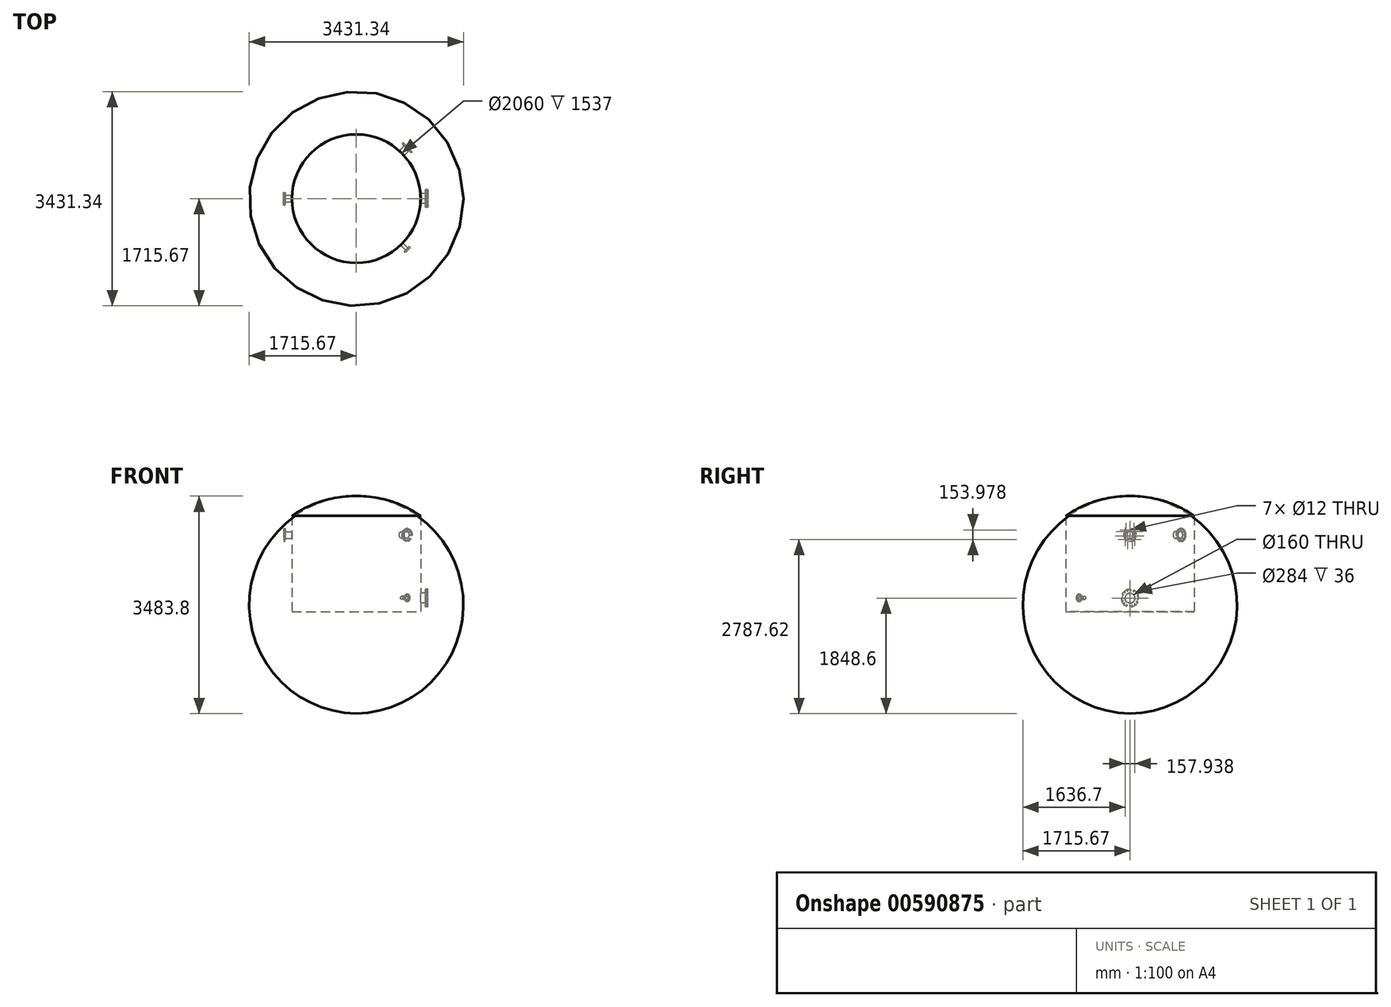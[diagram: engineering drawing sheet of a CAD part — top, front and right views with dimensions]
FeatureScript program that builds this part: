
annotation { "Feature Type Name" : "Feature", "Feature Type Description" : "" }
export const myFeature = defineFeature(function(context is Context, id is Id, definition is map)
    precondition{}
    {
        {
            var Q0;
            Q0=qCreatedBy(makeId("Front.planeOp"),FACE);
            var sketch = newSketch(context, id + "F0", { "sketchPlane" : qUnion([Q0])});
            skLineSegment(sketch, "E0", {"start": v(0, -113.2) * mm, "end": v(1030, -113.2) * mm});
            skLineSegment(sketch, "E1", {"start": v(1030, -113.2) * mm, "end": v(1030, 1423.8) * mm});
            skLineSegment(sketch, "E2", {"start": v(0, -329.04) * mm, "end": v(0, -113.2) * mm, "construction": true});
            skArc(sketch, "E3", {"start": v(1030, 1423.8) * mm, "mid": v(540.22, 1664.48) * mm, "end": v(0, 1741.8) * mm});
            skLineSegment(sketch, "E4", {"start": v(0, 1741.8) * mm, "end": v(0, -113.2) * mm});
            skSolve(sketch);
        }
        {
            var Q0;
            Q0 = qSketchRegion(id + "F0", true);
            var Q1;
            Q1=sQuery(id+"F0.wireOp",EDGE,"E2");
            revolve(context, id + "F1", {"entities" : qUnion([Q0]), "axis" : qUnion([Q1]), "revolveType" : RevolveType.FULL});
        }
        {
            var Q0;
            Q0=qCreatedBy(makeId("Right.planeOp"),FACE);
            cPlane(context, id + "F2", {"entities" : qUnion([Q0]), "cplaneType" : CPlaneType.OFFSET, "offset" : 1030 * mm, "width" : 150 * mm, "height" : 150 * mm});
        }
        {
            var Q0;
            Q0=qCreatedBy(id+"F2.planeOp",FACE);
            var sketch = newSketch(context, id + "F3", { "sketchPlane" : qUnion([Q0])});
            skCircle(sketch, "E5", {"center": v(0, 106.8) * mm, "radius": 80 * mm});
            skSolve(sketch);
        }
        {
            var Q0;
            Q0 = qSketchRegion(id + "F3", true);
            extrude(context, id + "F4", {"entities" : qUnion([Q0]), "operationType" : NewBodyOperationType.ADD, "endBound" : BoundingType.SYMMETRIC, "depth" : 160 * mm, "offsetDistance" : 25 * mm});
        }
        {
            var Q0;
            Q0=makeQuery(id+"F4.opExtrude","CAP_FACE",FACE,{"disambiguationData":[OSD([sQuery(id+"F3.wireOp",EDGE,"E5")])],"isStart":false});
            var sketch = newSketch(context, id + "F5", { "sketchPlane" : qUnion([Q0])});
            skCircle(sketch, "E6", {"center": v(0, 106.8) * mm, "radius": 142 * mm});
            skSolve(sketch);
        }
        {
            var Q0;
            Q0 = qSketchRegion(id + "F5", true);
            extrude(context, id + "F6", {"entities" : qUnion([Q0]), "operationType" : NewBodyOperationType.ADD, "depth" : 36 * mm, "offsetDistance" : 25 * mm});
        }
        {
            var Q0;
            Q0=makeQuery(id+"F6.opExtrude","CAP_FACE",FACE,{"disambiguationData":[OSD([sQuery(id+"F5.wireOp",EDGE,"E6")])],"isStart":false});
            var sketch = newSketch(context, id + "F7", { "sketchPlane" : qUnion([Q0])});
            skCircle(sketch, "E7", {"center": v(0, -18.2) * mm, "radius": 8 * mm});
            skCircle(sketch, "E8.1.0", {"center": v(-48.84, -8.26) * mm, "radius": 8 * mm});
            skCircle(sketch, "E8.2.0", {"center": v(-89.92, 19.97) * mm, "radius": 8 * mm});
            skCircle(sketch, "E8.3.0", {"center": v(-116.7, 62) * mm, "radius": 8 * mm});
            skCircle(sketch, "E8.4.0", {"center": v(-124.92, 111.16) * mm, "radius": 8 * mm});
            skCircle(sketch, "E8.5.0", {"center": v(-113.29, 159.63) * mm, "radius": 8 * mm});
            skCircle(sketch, "E8.6.0", {"center": v(-83.64, 199.7) * mm, "radius": 8 * mm});
            skCircle(sketch, "E8.7.0", {"center": v(-40.7, 225) * mm, "radius": 8 * mm});
            skCircle(sketch, "E8.8.0", {"center": v(8.72, 231.5) * mm, "radius": 8 * mm});
            skCircle(sketch, "E8.9.0", {"center": v(56.75, 218.18) * mm, "radius": 8 * mm});
            skCircle(sketch, "E8.10.0", {"center": v(95.76, 187.15) * mm, "radius": 8 * mm});
            skCircle(sketch, "E8.11.0", {"center": v(119.54, 143.35) * mm, "radius": 8 * mm});
            skCircle(sketch, "E8.12.0", {"center": v(124.32, 93.73) * mm, "radius": 8 * mm});
            skCircle(sketch, "E8.13.0", {"center": v(109.33, 46.2) * mm, "radius": 8 * mm});
            skCircle(sketch, "E8.14.0", {"center": v(76.96, 8.3) * mm, "radius": 8 * mm});
            skCircle(sketch, "E8.15.0", {"center": v(32.35, -13.94) * mm, "radius": 8 * mm});
            skPoint(sketch, "E8.center", {"position": v(0, 106.8) * mm});
            skLineSegment(sketch, "E8.anchor1", {"start": v(0, 106.8) * mm, "end": v(0, -18.2) * mm, "construction": true});
            skLineSegment(sketch, "E8.anchor2", {"start": v(0, 106.8) * mm, "end": v(32.35, -13.94) * mm, "construction": true});
            skSolve(sketch);
        }
        {
            var Q0;
            Q0 = qSketchRegion(id + "F7", true);
            extrude(context, id + "F8", {"entities" : qUnion([Q0]), "operationType" : NewBodyOperationType.REMOVE, "oppositeDirection" : true, "depth" : 75 * mm, "offsetDistance" : 25 * mm});
        }
        {
            var Q0;
            Q0=qCreatedBy(makeId("Right.planeOp"),FACE);
            cPlane(context, id + "F9", {"entities" : qUnion([Q0]), "cplaneType" : CPlaneType.OFFSET, "offset" : 1030 * mm, "oppositeDirection" : true, "width" : 150 * mm, "height" : 150 * mm});
        }
        {
            var Q0;
            Q0=qCreatedBy(id+"F9.planeOp",FACE);
            var sketch = newSketch(context, id + "F10", { "sketchPlane" : qUnion([Q0])});
            skCircle(sketch, "E9", {"center": v(0, 1118.8) * mm, "radius": 55 * mm});
            skSolve(sketch);
        }
        {
            var Q0;
            Q0 = qSketchRegion(id + "F10", true);
            extrude(context, id + "F11", {"entities" : qUnion([Q0]), "operationType" : NewBodyOperationType.ADD, "oppositeDirection" : true, "depth" : 110 * mm, "offsetDistance" : 25 * mm});
        }
        {
            var Q0;
            Q0=makeQuery(id+"F11.opExtrude","CAP_FACE",FACE,{"disambiguationData":[OSD([sQuery(id+"F10.wireOp",EDGE,"E9")])],"isStart":false});
            var sketch = newSketch(context, id + "F12", { "sketchPlane" : qUnion([Q0])});
            skCircle(sketch, "E10", {"center": v(0, 1118.8) * mm, "radius": 102 * mm});
            skSolve(sketch);
        }
        {
            var Q0;
            Q0 = qSketchRegion(id + "F12", true);
            extrude(context, id + "F13", {"entities" : qUnion([Q0]), "operationType" : NewBodyOperationType.ADD, "depth" : 25 * mm, "offsetDistance" : 25 * mm});
        }
        {
            var Q0;
            Q0=makeQuery(id+"F13.opExtrude","CAP_FACE",FACE,{"disambiguationData":[OSD([sQuery(id+"F12.wireOp",EDGE,"E10")])],"isStart":false});
            var sketch = newSketch(context, id + "F14", { "sketchPlane" : qUnion([Q0])});
            skCircle(sketch, "E11", {"center": v(0, 1199.8) * mm, "radius": 6 * mm});
            skCircle(sketch, "E12.1.0", {"center": v(-1039.06, -599.9) * mm, "radius": 6 * mm});
            skCircle(sketch, "E12.2.0", {"center": v(1039.06, -599.9) * mm, "radius": 6 * mm});
            skPoint(sketch, "E12.center", {"position": v(0, 0) * mm});
            skCircle(sketch, "E13.1.0", {"center": v(63.33, 1169.3) * mm, "radius": 6 * mm});
            skCircle(sketch, "E13.2.0", {"center": v(78.97, 1100.78) * mm, "radius": 6 * mm});
            skCircle(sketch, "E13.3.0", {"center": v(35.14, 1045.82) * mm, "radius": 6 * mm});
            skCircle(sketch, "E13.4.0", {"center": v(-35.14, 1045.82) * mm, "radius": 6 * mm});
            skCircle(sketch, "E13.5.0", {"center": v(-78.97, 1100.78) * mm, "radius": 6 * mm});
            skCircle(sketch, "E13.6.0", {"center": v(-63.33, 1169.3) * mm, "radius": 6 * mm});
            skPoint(sketch, "E13.center", {"position": v(0, 1118.8) * mm});
            skLineSegment(sketch, "E13.anchor1", {"start": v(0, 1118.8) * mm, "end": v(0, 1199.8) * mm, "construction": true});
            skLineSegment(sketch, "E13.anchor2", {"start": v(0, 1118.8) * mm, "end": v(0, 1199.8) * mm, "construction": true});
            skSolve(sketch);
        }
        {
            var Q0;
            Q0 = qSketchRegion(id + "F14", true);
            extrude(context, id + "F15", {"entities" : qUnion([Q0]), "operationType" : NewBodyOperationType.REMOVE, "oppositeDirection" : true, "depth" : 75 * mm, "offsetDistance" : 25 * mm});
        }
        {
            var Q0;
            Q0=qCreatedBy(makeId("Front.planeOp"),FACE);
            var Q1;
            Q1=makeQuery(id+"F1.opRevolve","SWEPT_FACE",FACE,{"disambiguationData":[OSD([sQuery(id+"F0.wireOp",EDGE,"E1")])]});
            cPlane(context, id + "F16", {"entities" : qUnion([Q0, Q1]), "cplaneType" : CPlaneType.LINE_ANGLE, "offset" : 25 * mm, "angle" : 45 * degree, "width" : 150 * mm, "height" : 150 * mm});
        }
        {
            var Q0;
            Q0=qCreatedBy(id+"F16.planeOp",FACE);
            cPlane(context, id + "F17", {"entities" : qUnion([Q0]), "cplaneType" : CPlaneType.OFFSET, "offset" : 1030 * mm, "width" : 150 * mm, "height" : 150 * mm});
        }
        {
            var Q0;
            Q0=qCreatedBy(id+"F17.planeOp",FACE);
            var sketch = newSketch(context, id + "F18", { "sketchPlane" : qUnion([Q0])});
            skCircle(sketch, "E14", {"center": v(0, 1118.8) * mm, "radius": 55 * mm});
            skSolve(sketch);
        }
        {
            var Q0;
            Q0 = qSketchRegion(id + "F18", true);
            extrude(context, id + "F19", {"entities" : qUnion([Q0]), "operationType" : NewBodyOperationType.ADD, "depth" : 110 * mm, "offsetDistance" : 25 * mm});
        }
        {
            var Q0;
            Q0=makeQuery(id+"F19.opExtrude","CAP_FACE",FACE,{"disambiguationData":[OSD([sQuery(id+"F18.wireOp",EDGE,"E14")])],"isStart":false});
            var sketch = newSketch(context, id + "F20", { "sketchPlane" : qUnion([Q0])});
            skCircle(sketch, "E15", {"center": v(0, 1118.8) * mm, "radius": 102 * mm});
            skSolve(sketch);
        }
        {
            var Q0;
            Q0 = qSketchRegion(id + "F20", true);
            extrude(context, id + "F21", {"entities" : qUnion([Q0]), "operationType" : NewBodyOperationType.ADD, "depth" : 25 * mm, "offsetDistance" : 25 * mm});
        }
        {
            var Q0;
            Q0=makeQuery(id+"F21.opExtrude","CAP_FACE",FACE,{"disambiguationData":[OSD([sQuery(id+"F20.wireOp",EDGE,"E15")])],"isStart":false});
            var sketch = newSketch(context, id + "F22", { "sketchPlane" : qUnion([Q0])});
            skCircle(sketch, "E16", {"center": v(0, 1205.8) * mm, "radius": 6 * mm});
            skCircle(sketch, "E17.1.0", {"center": v(-61.52, 1180.32) * mm, "radius": 6 * mm});
            skCircle(sketch, "E17.2.0", {"center": v(-87, 1118.8) * mm, "radius": 6 * mm});
            skCircle(sketch, "E17.3.0", {"center": v(-61.52, 1057.28) * mm, "radius": 6 * mm});
            skCircle(sketch, "E17.4.0", {"center": v(0, 1031.8) * mm, "radius": 6 * mm});
            skCircle(sketch, "E17.5.0", {"center": v(61.52, 1057.28) * mm, "radius": 6 * mm});
            skCircle(sketch, "E17.6.0", {"center": v(87, 1118.8) * mm, "radius": 6 * mm});
            skCircle(sketch, "E17.7.0", {"center": v(61.52, 1180.32) * mm, "radius": 6 * mm});
            skPoint(sketch, "E17.center", {"position": v(0, 1118.8) * mm});
            skSolve(sketch);
        }
        {
            var Q0;
            Q0 = qSketchRegion(id + "F22", true);
            extrude(context, id + "F23", {"entities" : qUnion([Q0]), "operationType" : NewBodyOperationType.REMOVE, "oppositeDirection" : true, "depth" : 75 * mm, "offsetDistance" : 25 * mm});
        }
        {
            var Q0;
            Q0=qCreatedBy(makeId("Front.planeOp"),FACE);
            var Q1;
            Q1=makeQuery(id+"F1.opRevolve","SWEPT_FACE",FACE,{"disambiguationData":[OSD([sQuery(id+"F0.wireOp",EDGE,"E1")])]});
            cPlane(context, id + "F24", {"entities" : qUnion([Q0, Q1]), "cplaneType" : CPlaneType.LINE_ANGLE, "offset" : 25 * mm, "angle" : 45 * degree, "oppositeDirection" : true, "width" : 150 * mm, "height" : 150 * mm});
        }
        {
            var Q0;
            Q0=qCreatedBy(id+"F24.planeOp",FACE);
            cPlane(context, id + "F25", {"entities" : qUnion([Q0]), "cplaneType" : CPlaneType.OFFSET, "offset" : 1030 * mm, "oppositeDirection" : true, "width" : 150 * mm, "height" : 150 * mm});
        }
        {
            var Q0;
            Q0=qCreatedBy(id+"F25.planeOp",FACE);
            var sketch = newSketch(context, id + "F26", { "sketchPlane" : qUnion([Q0])});
            skCircle(sketch, "E18", {"center": v(0, 111.8) * mm, "radius": 25 * mm});
            skSolve(sketch);
        }
        {
            var Q0;
            Q0 = qSketchRegion(id + "F26", true);
            extrude(context, id + "F27", {"entities" : qUnion([Q0]), "operationType" : NewBodyOperationType.ADD, "oppositeDirection" : true, "depth" : 110 * mm, "offsetDistance" : 25 * mm});
        }
        {
            var Q0;
            Q0=makeQuery(id+"F27.opExtrude","CAP_FACE",FACE,{"disambiguationData":[OSD([sQuery(id+"F26.wireOp",EDGE,"E18")])],"isStart":false});
            var sketch = newSketch(context, id + "F28", { "sketchPlane" : qUnion([Q0])});
            skCircle(sketch, "E19", {"center": v(0, 111.8) * mm, "radius": 55 * mm});
            skSolve(sketch);
        }
        {
            var Q0;
            Q0 = qSketchRegion(id + "F28", true);
            extrude(context, id + "F29", {"entities" : qUnion([Q0]), "operationType" : NewBodyOperationType.ADD, "depth" : 25 * mm, "offsetDistance" : 25 * mm});
        }
    });
